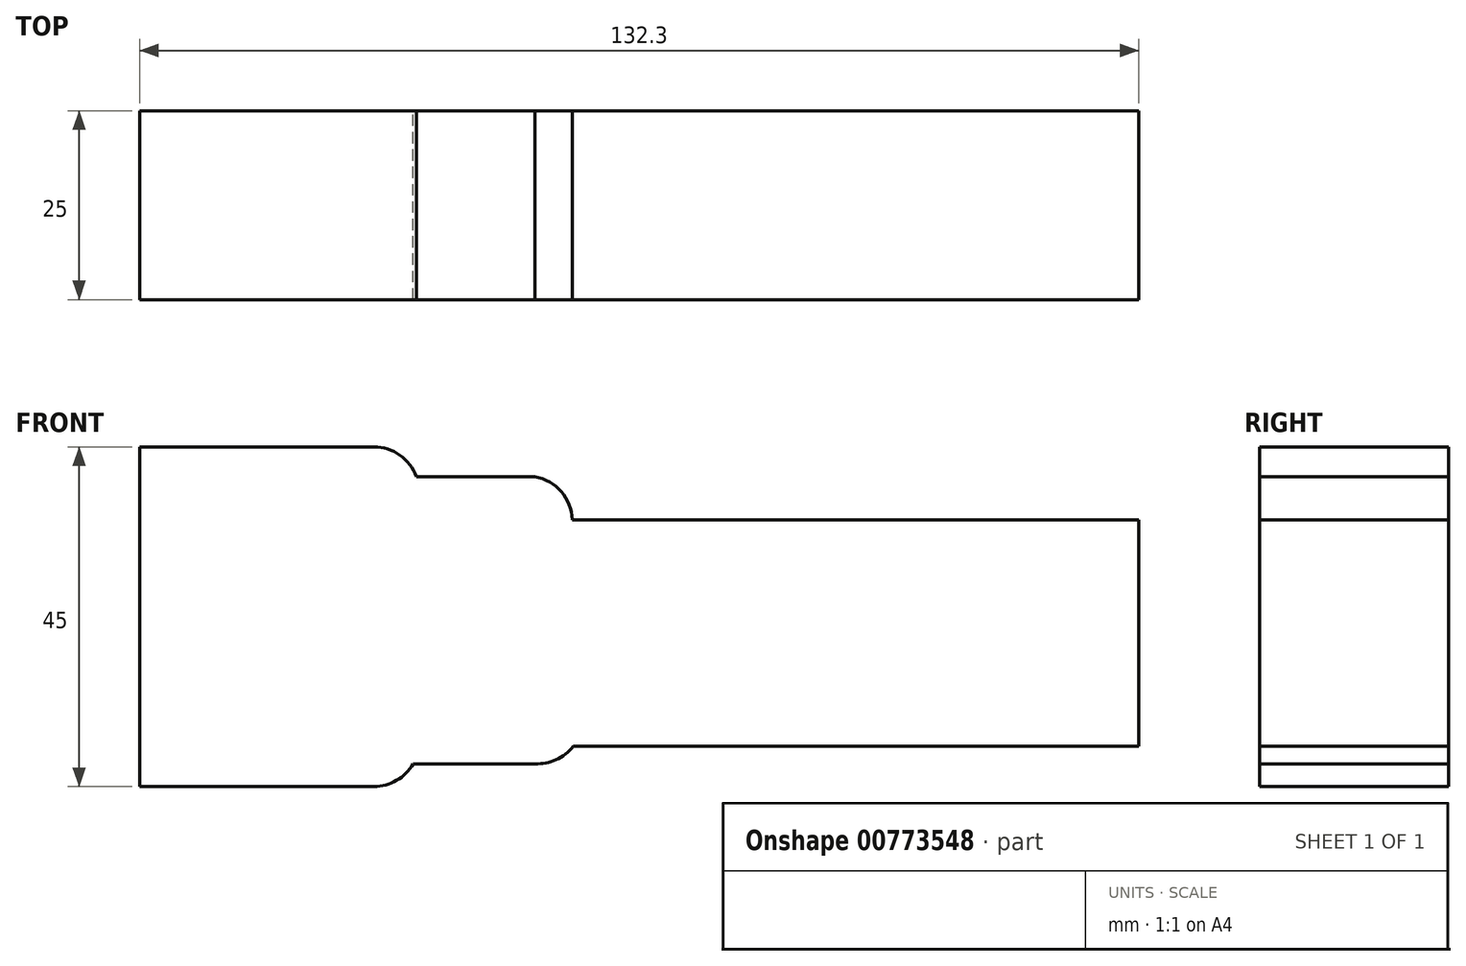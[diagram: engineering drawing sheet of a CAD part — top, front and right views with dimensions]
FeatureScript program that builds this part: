
annotation { "Feature Type Name" : "Feature", "Feature Type Description" : "" }
export const myFeature = defineFeature(function(context is Context, id is Id, definition is map)
    precondition{}
    {
        {
            var Q0;
            Q0=qCreatedBy(makeId("Front.planeOp"),FACE);
            var sketch = newSketch(context, id + "F0", { "sketchPlane" : qUnion([Q0])});
            skLineSegment(sketch, "E0", {"start": v(-102.41, 27.66) * mm, "end": v(-102.41, -17.34) * mm});
            skLineSegment(sketch, "E1", {"start": v(-71.4, -17.34) * mm, "end": v(-102.41, -17.34) * mm});
            skLineSegment(sketch, "E2", {"start": v(-102.41, 27.66) * mm, "end": v(-71.4, 27.66) * mm});
            skArc(sketch, "E3", {"start": v(-65.75, 23.69) * mm, "mid": v(-67.94, 26.57) * mm, "end": v(-71.4, 27.66) * mm});
            skArc(sketch, "E4", {"start": v(-71.4, -17.34) * mm, "mid": v(-68.38, -16.53) * mm, "end": v(-66.19, -14.31) * mm});
            skLineSegment(sketch, "E5", {"start": v(-65.75, 23.69) * mm, "end": v(-50.04, 23.69) * mm});
            skLineSegment(sketch, "E6", {"start": v(-66.19, -14.31) * mm, "end": v(-50.04, -14.31) * mm});
            skArc(sketch, "E7", {"start": v(-45.11, 18) * mm, "mid": v(-46.58, 21.71) * mm, "end": v(-50.04, 23.69) * mm});
            skLineSegment(sketch, "E8", {"start": v(-45.11, 18) * mm, "end": v(29.89, 18) * mm});
            skLineSegment(sketch, "E9", {"start": v(29.89, 18) * mm, "end": v(29.89, -12) * mm});
            skArc(sketch, "E10", {"start": v(-50.04, -14.31) * mm, "mid": v(-47.24, -13.77) * mm, "end": v(-45, -12) * mm});
            skLineSegment(sketch, "E11", {"start": v(-45, -12) * mm, "end": v(29.89, -12) * mm});
            skSolve(sketch);
        }
        {
            var Q0;
            Q0=makeQuery(id+"F0.imprint","IMPRINT",FACE,{"disambiguationData":[TD([[makeQuery(id+"F0.imprint","IMPRINT",EDGE,{"derivedFrom":sQuery(id+"F0.wireOp",EDGE,"E0")}),1.0]])]});
            extrude(context, id + "F1", {"entities" : qUnion([Q0]), "depth" : 25 * mm, "offsetDistance" : 25 * mm});
        }
    });
